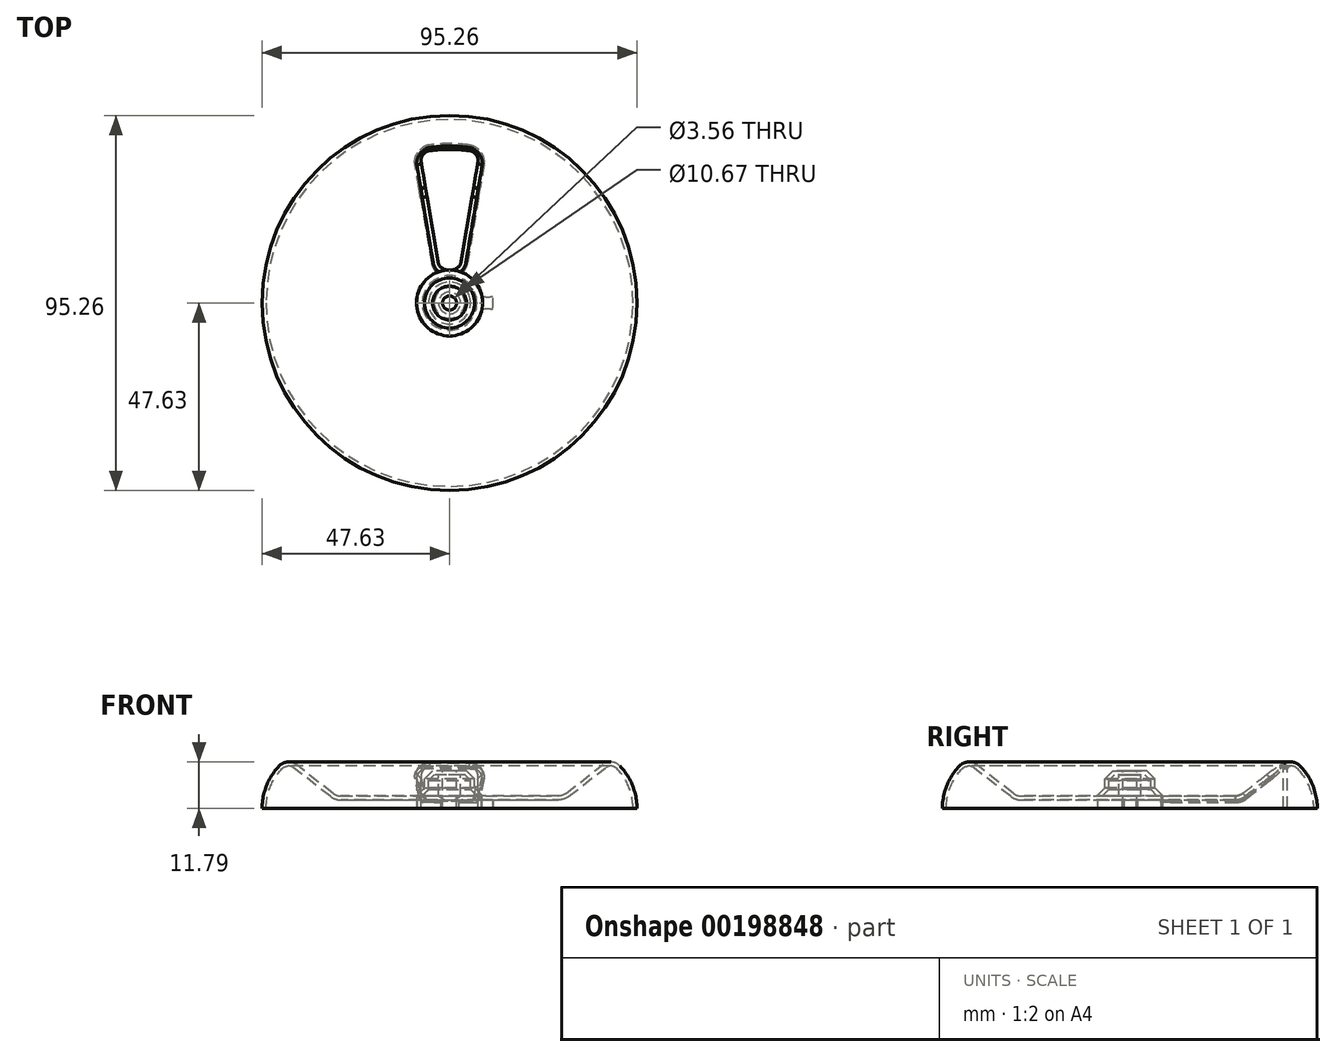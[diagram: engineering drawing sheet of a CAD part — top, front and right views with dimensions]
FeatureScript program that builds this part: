
annotation { "Feature Type Name" : "Feature", "Feature Type Description" : "" }
export const myFeature = defineFeature(function(context is Context, id is Id, definition is map)
    precondition{}
    {
        {
            var Q0;
            Q0=qCreatedBy(makeId("Right.planeOp"),FACE);
            var sketch = newSketch(context, id + "F0", { "sketchPlane" : qUnion([Q0])});
            skLineSegment(sketch, "E0", {"start": v(-1.78, 0) * mm, "end": v(-1.78, 9.53) * mm});
            skLineSegment(sketch, "E1", {"start": v(-1.78, 9.53) * mm, "end": v(-6.35, 9.53) * mm});
            skLineSegment(sketch, "E2", {"start": v(-6.35, 9.53) * mm, "end": v(-6.35, 3.18) * mm});
            skLineSegment(sketch, "E3", {"start": v(-6.35, 3.18) * mm, "end": v(-27.67, 3.18) * mm});
            skLineSegment(sketch, "E4", {"start": v(-29.62, 3.84) * mm, "end": v(-39.02, 11.12) * mm});
            skArc(sketch, "E5", {"start": v(-43.24, 10.82) * mm, "mid": v(-46.49, 5.84) * mm, "end": v(-47.63, 0) * mm});
            skLineSegment(sketch, "E6", {"start": v(-47.63, 0) * mm, "end": v(-1.78, 0) * mm});
            skPoint(sketch, "E7.visualSharp", {"position": v(-41.05, 12.7) * mm});
            skArc(sketch, "E7.filletArc", {"start": v(-39.02, 11.12) * mm, "mid": v(-41.19, 11.78) * mm, "end": v(-43.24, 10.82) * mm});
            skPoint(sketch, "E8.visualSharp", {"position": v(-28.76, 3.17) * mm});
            skArc(sketch, "E8.filletArc", {"start": v(-29.62, 3.84) * mm, "mid": v(-28.7, 3.35) * mm, "end": v(-27.67, 3.18) * mm});
            skLineSegment(sketch, "E9", {"start": v(0, 25.81) * mm, "end": v(0, -13.15) * mm, "construction": true});
            skSolve(sketch);
        }
        {
            var Q0;
            Q0 = qSketchRegion(id + "F0", true);
            var Q1;
            Q1=sQuery(id+"F0.wireOp",EDGE,"E9");
            revolve(context, id + "F1", {"entities" : qUnion([Q0]), "axis" : qUnion([Q1]), "revolveType" : RevolveType.FULL});
        }
        {
            var Q0;
            Q0=makeQuery(id+"F1.opRevolve","SWEPT_EDGE",EDGE,{"disambiguationData":[OSD([sQuery(id+"F0.wireOp",EDGE,"E2"),sQuery(id+"F0.wireOp",EDGE,"E3")])]});
            var Q1;
            Q1=makeQuery(id+"F1.opRevolve","SWEPT_EDGE",EDGE,{"disambiguationData":[OSD([sQuery(id+"F0.wireOp",EDGE,"E1"),sQuery(id+"F0.wireOp",EDGE,"E2")])]});
            chamfer(context, id + "F2", {"entities" : qUnion([Q0, Q1]), "width" : 2.03 * mm, "tangentPropagation" : true});
        }
        {
            var Q0;
            Q0=makeQuery(id+"F1.opRevolve","SWEPT_FACE",FACE,{"disambiguationData":[OSD([sQuery(id+"F0.wireOp",EDGE,"E3")])]});
            var sketch = newSketch(context, id + "F3", { "sketchPlane" : qUnion([Q0])});
            skArc(sketch, "E10.0", {"start": v(-2.54, 7.99) * mm, "mid": v(0, 8.38) * mm, "end": v(2.54, 7.99) * mm});
            skArc(sketch, "E11.0", {"start": v(7.62, 38.27) * mm, "mid": v(0, 39.02) * mm, "end": v(-7.62, 38.27) * mm});
            skLineSegment(sketch, "E12", {"start": v(0, 8.38) * mm, "end": v(0, 39.02) * mm, "construction": true});
            skLineSegment(sketch, "E13", {"start": v(-2.54, 7.99) * mm, "end": v(-7.62, 38.27) * mm});
            skLineSegment(sketch, "E14", {"start": v(2.54, 7.99) * mm, "end": v(7.62, 38.27) * mm});
            skSolve(sketch);
        }
        {
            var Q0;
            Q0 = qSketchRegion(id + "F3", true);
            extrude(context, id + "F4", {"entities" : qUnion([Q0]), "operationType" : NewBodyOperationType.REMOVE, "oppositeDirection" : true, "depth" : 25.4 * mm, "hasSecondDirection" : true, "secondDirectionOppositeDirection" : false, "secondDirectionDepth" : 25.4 * mm});
        }
        {
            var Q0;
            Q0=makeQuery(id+"F4.boolean.opBoolean","COPY",EDGE,{"derivedFrom":makeQuery(id+"F4.opExtrude","SWEPT_EDGE",EDGE,{"disambiguationData":[OSD([sQuery(id+"F3.wireOp",EDGE,"E11.0"),sQuery(id+"F3.wireOp",EDGE,"E13")])]})});
            var Q1;
            Q1=makeQuery(id+"F4.boolean.opBoolean","COPY",EDGE,{"derivedFrom":makeQuery(id+"F4.opExtrude","SWEPT_EDGE",EDGE,{"disambiguationData":[OSD([sQuery(id+"F3.wireOp",EDGE,"E11.0"),sQuery(id+"F3.wireOp",EDGE,"E14")])]})});
            var Q2;
            Q2=makeQuery(id+"F4.boolean.opBoolean","COPY",EDGE,{"derivedFrom":makeQuery(id+"F4.opExtrude","SWEPT_EDGE",EDGE,{"disambiguationData":[OSD([sQuery(id+"F0.wireOp",EDGE,"E2"),sQuery(id+"F0.wireOp",EDGE,"E3"),sQuery(id+"F3.wireOp",EDGE,"E10.0"),sQuery(id+"F3.wireOp",EDGE,"E14")])]})});
            var Q3;
            Q3=makeQuery(id+"F4.boolean.opBoolean","COPY",EDGE,{"derivedFrom":makeQuery(id+"F4.opExtrude","SWEPT_EDGE",EDGE,{"disambiguationData":[OSD([sQuery(id+"F0.wireOp",EDGE,"E2"),sQuery(id+"F0.wireOp",EDGE,"E3"),sQuery(id+"F3.wireOp",EDGE,"E10.0"),sQuery(id+"F3.wireOp",EDGE,"E13")])]})});
            fillet(context, id + "F5", {"entities" : qUnion([Q0, Q1, Q2, Q3]), "radius" : 2.54 * mm, "tangentPropagation" : true, "allowEdgeOverflow" : false});
        }
        {
            var Q0;
            Q0=makeQuery(id+"F4.boolean.opBoolean","INTERSECT",EDGE,{"derivedFrom":[makeQuery(id+"F1.opRevolve","SWEPT_FACE",FACE,{"disambiguationData":[OSD([sQuery(id+"F0.wireOp",EDGE,"E3")])]}),makeQuery(id+"F4.opExtrude","SWEPT_FACE",FACE,{"disambiguationData":[OSD([sQuery(id+"F3.wireOp",EDGE,"E13")])]})]});
            chamfer(context, id + "F6", {"entities" : qUnion([Q0]), "width" : 1.27 * mm, "tangentPropagation" : true});
        }
        {
            var Q0;
            Q0=makeQuery(id+"F1.opRevolve","SWEPT_FACE",FACE,{"disambiguationData":[OSD([sQuery(id+"F0.wireOp",EDGE,"E6")])]});
            shell(context, id + "F7", {"entities" : qUnion([Q0]), "thickness" : 1.02 * mm});
        }
        {
            var Q0;
            Q0=makeQuery(id+"F7.opShell","OFFSET_FACE",FACE,{"disambiguationData":[OSD([sQuery(id+"F0.wireOp",EDGE,"E6")]),OD(4.0)]});
            var sketch = newSketch(context, id + "F8", { "sketchPlane" : qUnion([Q0])});
            skCircle(sketch, "E15", {"center": v(0, 0) * mm, "radius": 8.2 * mm});
            skCircle(sketch, "E16", {"center": v(0, 0) * mm, "radius": 1.78 * mm});
            skSolve(sketch);
        }
        {
            var Q0;
            Q0 = qSketchRegion(id + "F8", true);
            extrude(context, id + "F9", {"entities" : qUnion([Q0]), "operationType" : NewBodyOperationType.ADD, "oppositeDirection" : true, "depth" : 3.17 * mm});
        }
        {
            var Q0;
            {var subQ0=sQuery(id+"F0.wireOp",EDGE,"E6");Q0=makeQuery(id+"F9.boolean.opBoolean","MERGE",FACE,{"derivedFrom":[makeQuery(id+"F1.opRevolve","SWEPT_FACE",FACE,{"disambiguationData":[OSD([subQ0])]}),makeQuery(id+"F7.opShell","OFFSET_FACE",FACE,{"disambiguationData":[OSD([subQ0]),OD(0.0)]}),makeQuery(id+"F7.opShell","OFFSET_FACE",FACE,{"disambiguationData":[OSD([subQ0]),OD(2.0)]}),makeQuery(id+"F7.opShell","OFFSET_FACE",FACE,{"disambiguationData":[OSD([subQ0]),OD(3.0)]}),makeQuery(id+"F7.opShell","OFFSET_FACE",FACE,{"disambiguationData":[OSD([subQ0]),OD(4.0)]}),makeQuery(id+"F7.opShell","OFFSET_FACE",FACE,{"disambiguationData":[OSD([subQ0]),OD(5.0)]}),makeQuery(id+"F7.opShell","OFFSET_FACE",FACE,{"disambiguationData":[OSD([subQ0]),OD(6.0)]}),makeQuery(id+"F9.opExtrude","CAP_FACE",FACE,{"disambiguationData":[OSD([sQuery(id+"F8.wireOp",EDGE,"E15"),sQuery(id+"F8.wireOp",EDGE,"E16")])],"isStart":true})]});}
            var sketch = newSketch(context, id + "F10", { "sketchPlane" : qUnion([Q0])});
            skArc(sketch, "E17", {"start": v(10.92, -1.73) * mm, "mid": v(11.06, 0) * mm, "end": v(10.92, 1.73) * mm});
            skArc(sketch, "E18.0", {"start": v(10.92, 1.73) * mm, "mid": v(9.42, 1.52) * mm, "end": v(7.97, 1.95) * mm});
            skArc(sketch, "E18.1", {"start": v(7.97, -1.95) * mm, "mid": v(9.42, -1.52) * mm, "end": v(10.92, -1.73) * mm});
            skArc(sketch, "E18.2", {"start": v(7.97, -1.95) * mm, "mid": v(8.2, 0) * mm, "end": v(7.97, 1.95) * mm});
            skSolve(sketch);
        }
        {
            var Q0;
            Q0 = qSketchRegion(id + "F10", true);
            extrude(context, id + "F11", {"entities" : qUnion([Q0]), "operationType" : NewBodyOperationType.ADD, "endBound" : BoundingType.UP_TO_NEXT, "oppositeDirection" : true, "depth" : 25.4 * mm});
        }
    });
